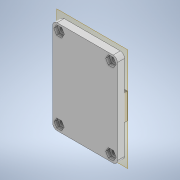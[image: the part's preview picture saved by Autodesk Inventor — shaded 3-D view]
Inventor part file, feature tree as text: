
AUTODESK INVENTOR PART (.ipt)
format: ipt  version: 2021.2 (Build 252289000, 289)  size: 212,480 bytes
history: native  units: mm
features: other x6, extrude x5, sketch x5, reference x3
ambient origin geometry x8: Origin, YZ Plane, XZ Plane, XY Plane, X Axis, Y Axis, Z Axis, Center Point
bodies: Body1 (feature_tree)
feature tree (19):
  other  "Твердое тело1"
  other  "РабПлоскость1"
  extrude  "Выдавливание1"  Depth=4.0mm TaperAngle=0.0deg
  sketch  "Эскиз2"
  extrude  "Выдавливание2"  Depth=6.3mm
  extrude  "Выдавливание3"  Depth=1.0mm TaperAngle=0.0deg
  extrude  "Выдавливание4"  Depth=1.0mm TaperAngle=0.0deg
  extrude  "Выдавливание5"  Depth=40.5mm
  sketch  "Эскиз1"
  reference  "Ссылка1"
  sketch  "Эскиз3"
  sketch  "Эскиз4"
  sketch  "Эскиз5"
  reference  "Ссылка2"
  reference  "Ссылка3"
  other  "Сборка1"
  other  "level1_up:1"
  other  "plate:1"
  other  "level3_up:1"
